# Revit family: Lift-Savaria_Vuelift_Round-Mini-3-Story
name_source: partatom
category: Generic Models
units: mm (PartAtom-declared; Revit-internal decimal feet)

## family parameters
Always vertical = Yes
Can host rebar = No
Classification Number = 23.50.05.14
Cut with Voids When Loaded = No
Maintain Annotation Orientation = No
Part Type = Normal
Room Calculation Point = No
Round Connector Dimension = Use Diameter
Shared = No
Work Plane-Based = No

## types (3) — shared parameters
78" H Cab = 78"
Applied Code = ASME 17.1-2013 SEC. 5.3
Cabin Flooring Material = <By Category>
Cabinet Floor Area = 39", 8.25 ft2, 1m, 0.75 m2
Cabinet Interior Height = 78'' [1.98 m]
Cabinet Weight = 550 lb 250 kg
Capacity = 500lbs [227 kg]
Classification = Residential Building
Default Elevation = 0"
Glass = Glass
Hoistway Door = 78"
Manufacturer = Savaria
Model = Round Mini Acrylic
Number of Floors = 3 Max.
Power Supply = 60 Hz Single Phase 240 volt (60Hz)
Specification = https://276ajivls9v24coqa255x2fb-wpengine.netdna-ssl.com
URL = https://www.savaria.com
Walls = Clear Acrylic - ANSI Z97.1

## per-type parameters (varying)
| type | Frame |
| Round Mini - Black Sandtex | Powder Coat - Savaria - Black Sandtex |
| Round Mini - Silver Sandtex | Powder Coat - Savaria - Silver Sandtex |
| Round Mini - White Sandtex | Powder Coat - Savaria - White Sandtex |

## geometry (parser evidence)
native form markers: Sweep x19
no freeform markers — native parametric forms only
